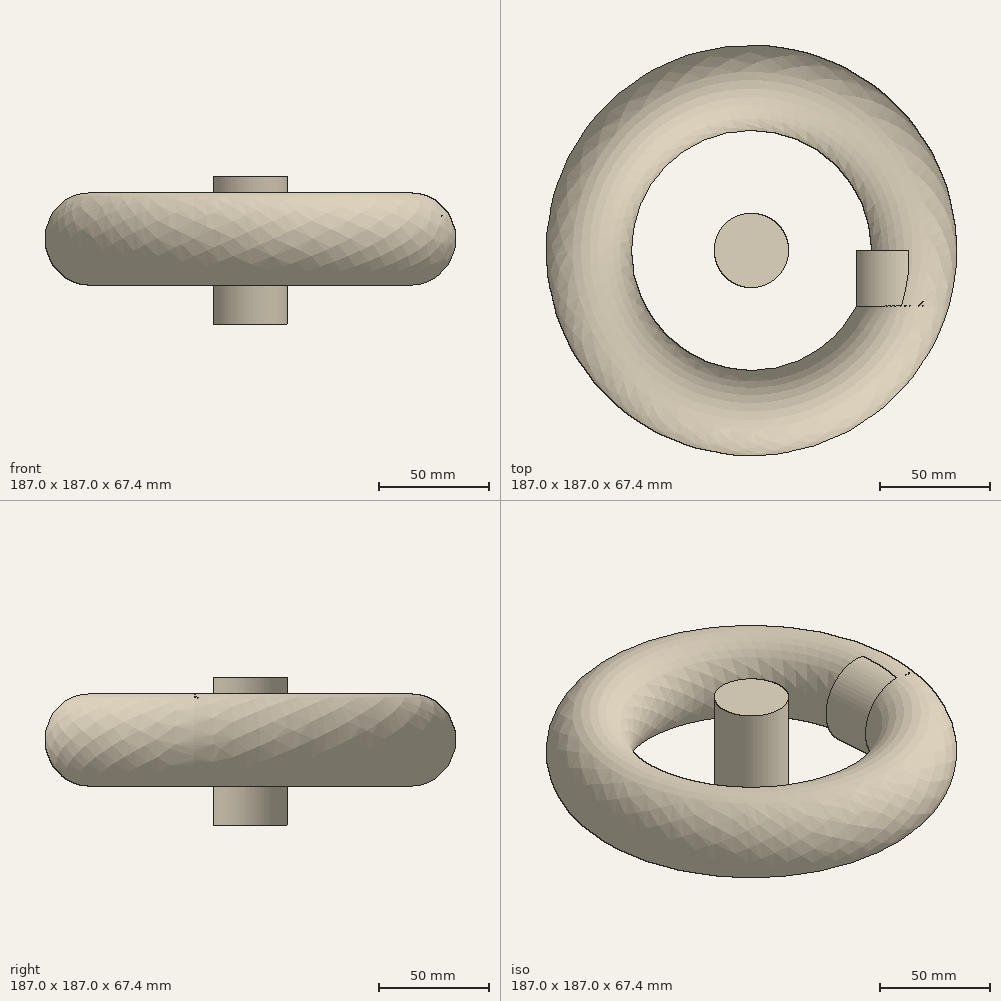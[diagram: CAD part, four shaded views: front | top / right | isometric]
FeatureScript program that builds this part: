
annotation { "Feature Type Name" : "Feature", "Feature Type Description" : "" }
export const myFeature = defineFeature(function(context is Context, id is Id, definition is map)
    precondition{}
    {
        {
            var Q0;
            Q0=qCreatedBy(makeId("Front.planeOp"),FACE);
            var sketch = newSketch(context, id + "F0", { "sketchPlane" : qUnion([Q0])});
            skLineSegment(sketch, "E0.bottom", {"start": v(-32.43, 45.76) * mm, "end": v(-15.5, 45.76) * mm});
            skLineSegment(sketch, "E0.top", {"start": v(-32.43, -21.62) * mm, "end": v(-15.5, -21.62) * mm});
            skLineSegment(sketch, "E0.left", {"start": v(-32.43, 45.76) * mm, "end": v(-32.43, -21.62) * mm});
            skLineSegment(sketch, "E0.right", {"start": v(-15.5, 45.76) * mm, "end": v(-15.5, -21.62) * mm});
            skLineSegment(sketch, "E1", {"start": v(-10.45, 66.3) * mm, "end": v(-10.45, -51.88) * mm});
            skCircle(sketch, "E2", {"center": v(36.57, 17.3) * mm, "radius": 20.99 * mm});
            skLineSegment(sketch, "E3", {"start": v(36.57, 17.3) * mm, "end": v(36.57, -3.7) * mm});
            skCircle(sketch, "E4", {"center": v(8.63, 213.65) * mm, "radius": 20.99 * mm});
            skCircle(sketch, "E5", {"center": v(-4.55, 197.32) * mm, "radius": 14.63 * mm});
            skCircle(sketch, "E6", {"center": v(0, 171.86) * mm, "radius": 84.9 * mm});
            skLineSegment(sketch, "E7", {"start": v(-15.92, 255.25) * mm, "end": v(105.41, 174.36) * mm});
            skLineSegment(sketch, "E8", {"start": v(0, 183.42) * mm, "end": v(92.11, 213.54) * mm});
            skLineSegment(sketch, "E9", {"start": v(25.41, 201.04) * mm, "end": v(-6.48, 177.82) * mm});
            skLineSegment(sketch, "E10", {"start": v(9.47, 192.68) * mm, "end": v(126.06, 197.32) * mm});
            skPoint(sketch, "E10.startSnap0", {"position": v(9.47, 189.43) * mm});
            skLineSegment(sketch, "E11", {"start": v(0, 211.22) * mm, "end": v(120.32, 171.87) * mm});
            skLineSegment(sketch, "E12", {"start": v(-10.93, 221.26) * mm, "end": v(-28.04, 177.27) * mm});
            skSolve(sketch);
        }
        {
            var Q0;
            Q0=makeQuery(id+"F0.imprint","IMPRINT",FACE,{"disambiguationData":[TD([[makeQuery(id+"F0.imprint","IMPRINT",EDGE,{"derivedFrom":sQuery(id+"F0.wireOp",EDGE,"E0.bottom")}),-1.0]])]});
            var Q1;
            Q1=sQuery(id+"F0.wireOp",EDGE,"E0.right");
            var Q2;
            Q2=sQuery(id+"F0.wireOp",EDGE,"E0.left");
            revolve(context, id + "F1", {"entities" : qUnion([Q0]), "surfaceEntities" : qUnion([Q1]), "axis" : qUnion([Q2]), "revolveType" : RevolveType.FULL});
        }
        {
            var Q0;
            Q0=makeQuery(id+"F0.imprint","IMPRINT",FACE,{"disambiguationData":[TD([[makeQuery(id+"F0.imprint","IMPRINT",EDGE,{"derivedFrom":sQuery(id+"F0.wireOp",EDGE,"E2")}),1.0]])]});
            extrude(context, id + "F2", {"entities" : qUnion([Q0]), "depth" : 25.4 * mm});
        }
        {
            var Q0;
            Q0=makeQuery(id+"F2.opExtrude","CAP_FACE",FACE,{"disambiguationData":[OSD([sQuery(id+"F0.wireOp",EDGE,"E2")])],"isStart":false});
            var Q1;
            Q1=makeQuery(id+"F2.opExtrude","CAP_EDGE",EDGE,{"disambiguationData":[OSD([sQuery(id+"F0.wireOp",EDGE,"E2")])],"isStart":false});
            var Q2;
            Q2=makeQuery(id+"F1.opRevolve","SWEPT_FACE",FACE,{"disambiguationData":[OSD([sQuery(id+"F0.wireOp",EDGE,"E0.right")])]});
            revolve(context, id + "F3", {"entities" : qUnion([Q0]), "surfaceEntities" : qUnion([Q1]), "axis" : qUnion([Q2]), "revolveType" : RevolveType.FULL});
        }
    });
